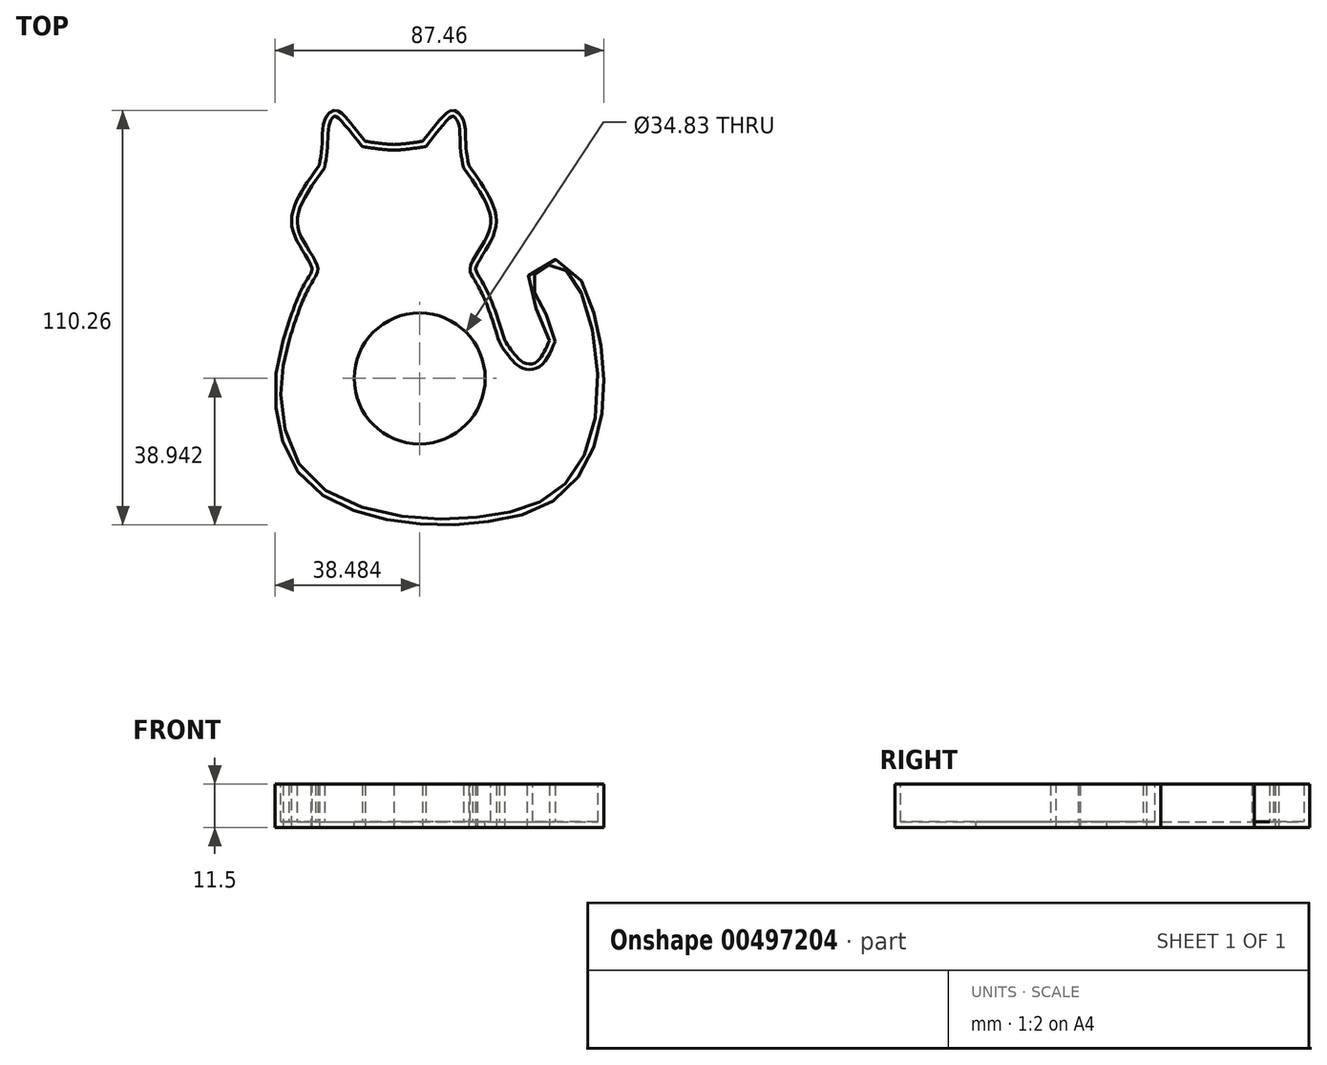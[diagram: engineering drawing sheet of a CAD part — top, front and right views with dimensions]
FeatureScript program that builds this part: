
annotation { "Feature Type Name" : "Feature", "Feature Type Description" : "" }
export const myFeature = defineFeature(function(context is Context, id is Id, definition is map)
    precondition{}
    {
        {
            var Q0;
            Q0=qCreatedBy(makeId("Top.planeOp"),FACE);
            var sketch = newSketch(context, id + "F0", { "sketchPlane" : qUnion([Q0])});
            skFitSpline(sketch, "E0", {"points": [v(-30, 14.48) * mm, v(-29.4, 16.9) * mm, v(-33.6, 24.73) * mm, v(-34.51, 31.66) * mm, v(-27.58, 43.4) * mm], "startDerivative": vector(8.24, 14.32) * mm, "endDerivative": vector(26.46, 36.86) * mm});
            skFitSpline(sketch, "E1", {"points": [v(-27.58, 43.4) * mm, v(-26.75, 49.48) * mm, v(-26.23, 55.36) * mm, v(-25.08, 57.04) * mm, v(-24.54, 57.14) * mm, v(-17.57, 49.08) * mm], "startDerivative": vector(4.48, 24.54) * mm, "endDerivative": vector(28.25, -36.07) * mm});
            skFitSpline(sketch, "E2", {"points": [v(-17.57, 49.08) * mm, v(-12.54, 48.36) * mm, v(-9.1, 48.08) * mm], "startDerivative": vector(9.6, -1.5) * mm, "endDerivative": vector(7.26, -0.46) * mm});
            skFitSpline(sketch, "E3", {"points": [v(-30, 14.48) * mm, v(-33.06, 8.82) * mm, v(-37.11, -2.83) * mm], "startDerivative": vector(-7.37, -12.12) * mm, "endDerivative": vector(-6.89, -21.98) * mm});
            skFitSpline(sketch, "E4.MirrorCS", {"points": [v(-0.63, 49.08) * mm, v(-5.66, 48.36) * mm, v(-9.1, 48.08) * mm], "startDerivative": vector(-9.6, -1.5) * mm, "endDerivative": vector(-7.26, -0.46) * mm});
            skFitSpline(sketch, "E5.MirrorCS", {"points": [v(11.8, 14.48) * mm, v(11.2, 16.9) * mm, v(15.4, 24.73) * mm, v(16.31, 31.66) * mm, v(9.38, 43.4) * mm], "startDerivative": vector(-8.24, 14.32) * mm, "endDerivative": vector(-26.46, 36.86) * mm});
            skFitSpline(sketch, "E6.MirrorCS", {"points": [v(9.38, 43.4) * mm, v(8.54, 49.48) * mm, v(8.03, 55.36) * mm, v(6.88, 57.04) * mm, v(6.34, 57.14) * mm, v(-0.63, 49.08) * mm], "startDerivative": vector(-4.48, 24.54) * mm, "endDerivative": vector(-28.25, -36.07) * mm});
            skFitSpline(sketch, "E7.MirrorCS", {"points": [v(11.8, 14.48) * mm, v(14.86, 8.82) * mm, v(18.91, -2.83) * mm], "startDerivative": vector(7.37, -12.12) * mm, "endDerivative": vector(6.89, -21.98) * mm});
            skFitSpline(sketch, "E8", {"points": [v(-37.11, -2.83) * mm, v(-39.23, -15.4) * mm, v(-32.65, -37.69) * mm, v(-6.8, -49.34) * mm, v(18.03, -48.84) * mm, v(34.75, -42.25) * mm, v(44.89, -20.46) * mm, v(40.33, 10.96) * mm, v(33.74, 17.55) * mm, v(28.67, 15.52) * mm, v(28.64, 9.36) * mm, v(33.74, -2.83) * mm], "startDerivative": vector(-38.2, -142.6) * mm, "endDerivative": vector(9.25, -195.73) * mm});
            skFitSpline(sketch, "E9", {"points": [v(18.91, -2.83) * mm, v(21.58, -6.78) * mm, v(24.87, -9.76) * mm, v(29.69, -9.46) * mm, v(33.74, -2.83) * mm], "startDerivative": vector(8.27, -18.25) * mm, "endDerivative": vector(8.2, 20.64) * mm});
            skSolve(sketch);
        }
        {
            var Q0;
            Q0 = qSketchRegion(id + "F0", true);
            extrude(context, id + "F1", {"entities" : qUnion([Q0]), "depth" : 10 * mm});
        }
        {
            var Q0;
            Q0=makeQuery(id+"F1.opExtrude","CAP_FACE",FACE,{"disambiguationData":[OSD([sQuery(id+"F0.wireOp",EDGE,"E0"),sQuery(id+"F0.wireOp",EDGE,"E1"),sQuery(id+"F0.wireOp",EDGE,"E2"),sQuery(id+"F0.wireOp",EDGE,"E3"),sQuery(id+"F0.wireOp",EDGE,"E4.MirrorCS"),sQuery(id+"F0.wireOp",EDGE,"E5.MirrorCS"),sQuery(id+"F0.wireOp",EDGE,"E6.MirrorCS"),sQuery(id+"F0.wireOp",EDGE,"E7.MirrorCS"),sQuery(id+"F0.wireOp",EDGE,"E8"),sQuery(id+"F0.wireOp",EDGE,"E9")])],"isStart":false});
            shell(context, id + "F2", {"entities" : qUnion([Q0]), "thickness" : 1.5 * mm, "oppositeDirection" : true});
        }
        {
            var Q0;
            Q0=makeQuery(id+"F2.opShell","OFFSET_FACE",FACE,{"disambiguationData":[OSD([sQuery(id+"F0.wireOp",EDGE,"E0"),sQuery(id+"F0.wireOp",EDGE,"E1"),sQuery(id+"F0.wireOp",EDGE,"E2"),sQuery(id+"F0.wireOp",EDGE,"E3"),sQuery(id+"F0.wireOp",EDGE,"E4.MirrorCS"),sQuery(id+"F0.wireOp",EDGE,"E5.MirrorCS"),sQuery(id+"F0.wireOp",EDGE,"E6.MirrorCS"),sQuery(id+"F0.wireOp",EDGE,"E7.MirrorCS"),sQuery(id+"F0.wireOp",EDGE,"E8"),sQuery(id+"F0.wireOp",EDGE,"E9")])]});
            var sketch = newSketch(context, id + "F3", { "sketchPlane" : qUnion([Q0])});
            skCircle(sketch, "E10", {"center": v(-2.26, -12.63) * mm, "radius": 17.41 * mm});
            skSolve(sketch);
        }
        {
            var Q0;
            Q0=makeQuery(id+"F3.imprint","IMPRINT",FACE,{"disambiguationData":[TD([[makeQuery(id+"F3.imprint","IMPRINT",EDGE,{"derivedFrom":sQuery(id+"F3.wireOp",EDGE,"E10")}),1.0]])]});
            extrude(context, id + "F4", {"entities" : qUnion([Q0]), "operationType" : NewBodyOperationType.REMOVE, "oppositeDirection" : true, "depth" : 25 * mm});
        }
    });
